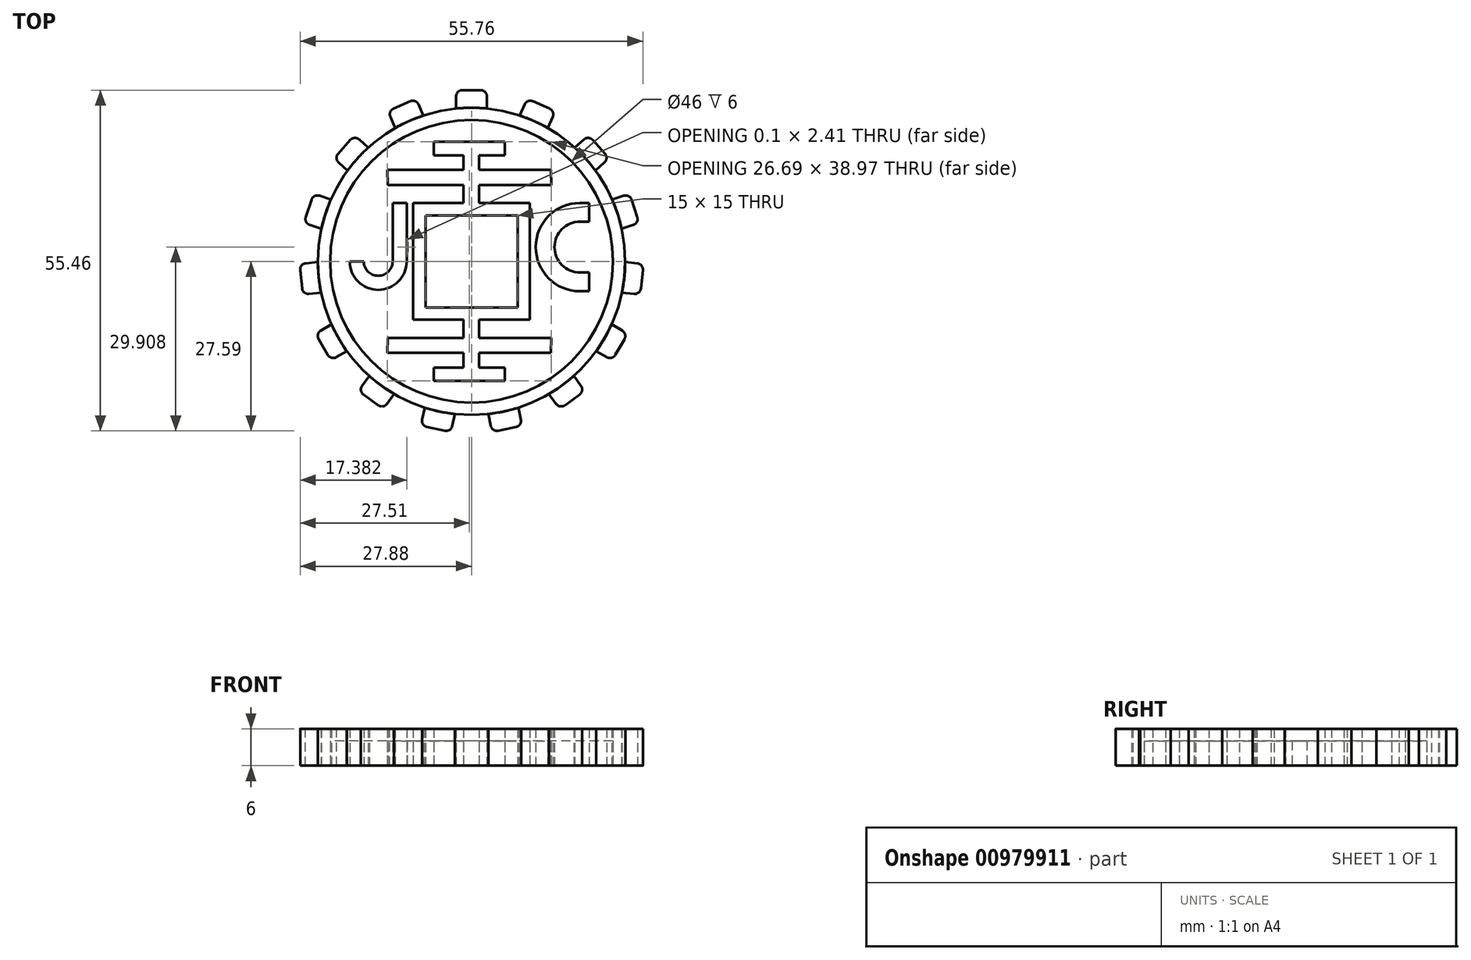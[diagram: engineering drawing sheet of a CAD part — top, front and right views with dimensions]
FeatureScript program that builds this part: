
annotation { "Feature Type Name" : "Feature", "Feature Type Description" : "" }
export const myFeature = defineFeature(function(context is Context, id is Id, definition is map)
    precondition{}
    {
        {
            var Q0;
            Q0=qCreatedBy(makeId("Top.planeOp"),FACE);
            var sketch = newSketch(context, id + "F0", { "sketchPlane" : qUnion([Q0])});
            skLineSegment(sketch, "E0.bottom", {"start": v(7.5, 7.5) * mm, "end": v(-7.5, 7.5) * mm});
            skLineSegment(sketch, "E0.top", {"start": v(7.5, -7.5) * mm, "end": v(-7.5, -7.5) * mm});
            skLineSegment(sketch, "E0.left", {"start": v(7.5, 7.5) * mm, "end": v(7.5, -7.5) * mm});
            skLineSegment(sketch, "E0.right", {"start": v(-7.5, 7.5) * mm, "end": v(-7.5, -7.5) * mm});
            skPoint(sketch, "E0.middle", {"position": v(0, 0) * mm});
            skLineSegment(sketch, "E1.bottom", {"start": v(9.5, 9.5) * mm, "end": v(-9.5, 9.5) * mm});
            skLineSegment(sketch, "E1.top", {"start": v(9.5, -9.5) * mm, "end": v(-9.5, -9.5) * mm});
            skLineSegment(sketch, "E1.left", {"start": v(9.5, 9.5) * mm, "end": v(9.5, -9.5) * mm});
            skLineSegment(sketch, "E1.right", {"start": v(-9.5, 9.5) * mm, "end": v(-9.5, -9.5) * mm});
            skCircle(sketch, "E2", {"center": v(0, 0) * mm, "radius": 25 * mm});
            skCircle(sketch, "E3", {"center": v(0, 0) * mm, "radius": 23 * mm});
            skLineSegment(sketch, "E4", {"start": v(-13.71, 14.88) * mm, "end": v(12.88, 14.88) * mm});
            skLineSegment(sketch, "E5", {"start": v(0, -9.5) * mm, "end": v(0, -9.5) * mm});
            skLineSegment(sketch, "E6", {"start": v(-13.64, 12.45) * mm, "end": v(12.97, 12.45) * mm});
            skLineSegment(sketch, "E7", {"start": v(-13.64, 12.45) * mm, "end": v(-13.71, 14.88) * mm});
            skLineSegment(sketch, "E8", {"start": v(12.88, 14.88) * mm, "end": v(12.97, 12.45) * mm});
            skLineSegment(sketch, "E9.bottom", {"start": v(-1.34, 12.45) * mm, "end": v(1.23, 12.45) * mm});
            skLineSegment(sketch, "E9.top", {"start": v(-1.34, 17.28) * mm, "end": v(1.23, 17.28) * mm});
            skLineSegment(sketch, "E9.left", {"start": v(-1.34, 12.45) * mm, "end": v(-1.34, 17.28) * mm});
            skLineSegment(sketch, "E9.right", {"start": v(1.23, 12.45) * mm, "end": v(1.23, 17.28) * mm});
            skLineSegment(sketch, "E10.bottom", {"start": v(1.23, 17.28) * mm, "end": v(-6.17, 17.28) * mm});
            skLineSegment(sketch, "E10.top", {"start": v(1.23, 19.48) * mm, "end": v(-6.17, 19.48) * mm});
            skLineSegment(sketch, "E10.left", {"start": v(1.23, 17.28) * mm, "end": v(1.23, 19.48) * mm});
            skLineSegment(sketch, "E10.right", {"start": v(-6.17, 17.28) * mm, "end": v(-6.17, 19.48) * mm});
            skLineSegment(sketch, "E11.bottom", {"start": v(-1.34, 17.28) * mm, "end": v(5.39, 17.28) * mm});
            skLineSegment(sketch, "E11.top", {"start": v(-1.34, 19.48) * mm, "end": v(5.39, 19.48) * mm});
            skLineSegment(sketch, "E11.left", {"start": v(-1.34, 17.28) * mm, "end": v(-1.34, 19.48) * mm});
            skLineSegment(sketch, "E11.right", {"start": v(5.39, 17.28) * mm, "end": v(5.39, 19.48) * mm});
            skLineSegment(sketch, "E12", {"start": v(-1.34, 12.45) * mm, "end": v(-1.34, 9.5) * mm});
            skLineSegment(sketch, "E13", {"start": v(1.23, 12.45) * mm, "end": v(1.23, 9.5) * mm});
            skLineSegment(sketch, "E14.MirrorCS", {"start": v(-1.34, -12.45) * mm, "end": v(-1.34, -9.5) * mm});
            skLineSegment(sketch, "E15.MirrorCS", {"start": v(1.23, -12.45) * mm, "end": v(1.23, -9.5) * mm});
            skLineSegment(sketch, "E16.MirrorCS", {"start": v(1.23, -12.45) * mm, "end": v(1.23, -17.28) * mm});
            skLineSegment(sketch, "E17.MirrorCS", {"start": v(-1.34, -12.45) * mm, "end": v(-1.34, -17.28) * mm});
            skLineSegment(sketch, "E18.MirrorCS", {"start": v(-13.64, -12.45) * mm, "end": v(-13.71, -14.88) * mm});
            skLineSegment(sketch, "E19.MirrorCS", {"start": v(12.88, -14.88) * mm, "end": v(12.97, -12.45) * mm});
            skLineSegment(sketch, "E20.MirrorCS", {"start": v(5.39, -17.28) * mm, "end": v(5.39, -19.48) * mm});
            skLineSegment(sketch, "E21.MirrorCS", {"start": v(-6.17, -17.28) * mm, "end": v(-6.17, -19.48) * mm});
            skLineSegment(sketch, "E22.MirrorCS", {"start": v(1.23, -19.48) * mm, "end": v(-6.17, -19.48) * mm});
            skLineSegment(sketch, "E23.MirrorCS", {"start": v(-1.34, -17.28) * mm, "end": v(-1.34, -19.48) * mm});
            skLineSegment(sketch, "E24.MirrorCS", {"start": v(1.23, -17.28) * mm, "end": v(1.23, -19.48) * mm});
            skLineSegment(sketch, "E25.MirrorCS", {"start": v(-1.34, -19.48) * mm, "end": v(5.39, -19.48) * mm});
            skLineSegment(sketch, "E26.MirrorCS", {"start": v(1.23, -17.28) * mm, "end": v(-6.17, -17.28) * mm});
            skLineSegment(sketch, "E27.MirrorCS", {"start": v(-1.34, -17.28) * mm, "end": v(5.39, -17.28) * mm});
            skLineSegment(sketch, "E28.MirrorCS", {"start": v(-13.71, -14.88) * mm, "end": v(12.88, -14.88) * mm});
            skLineSegment(sketch, "E29.MirrorCS", {"start": v(-13.64, -12.45) * mm, "end": v(12.97, -12.45) * mm});
            skLineSegment(sketch, "E30", {"start": v(-12.83, 9.5) * mm, "end": v(-12.83, 0) * mm});
            skLineSegment(sketch, "E31", {"start": v(-10.55, 9.5) * mm, "end": v(-10.55, 0) * mm});
            skLineSegment(sketch, "E32", {"start": v(-12.83, 9.5) * mm, "end": v(-10.55, 9.5) * mm});
            skLineSegment(sketch, "E33", {"start": v(19.13, 9.5) * mm, "end": v(19.13, 6.44) * mm});
            skLineSegment(sketch, "E34", {"start": v(19.13, 9.5) * mm, "end": v(17.63, 9.5) * mm});
            skArc(sketch, "E35", {"start": v(17.63, 9.5) * mm, "mid": v(10.45, 2.32) * mm, "end": v(17.63, -4.86) * mm});
            skArc(sketch, "E36.0", {"start": v(17.63, 6.45) * mm, "mid": v(13.5, 2.32) * mm, "end": v(17.63, -1.82) * mm});
            skLineSegment(sketch, "E37", {"start": v(17.63, 6.45) * mm, "end": v(19.13, 6.44) * mm});
            skLineSegment(sketch, "E38", {"start": v(17.63, -1.82) * mm, "end": v(19.13, -1.82) * mm});
            skLineSegment(sketch, "E39", {"start": v(17.63, -4.86) * mm, "end": v(19.13, -4.86) * mm});
            skLineSegment(sketch, "E40", {"start": v(19.13, -1.82) * mm, "end": v(19.13, -4.86) * mm});
            skArc(sketch, "E41", {"start": v(-10.55, 0) * mm, "mid": v(-15.18, -4.63) * mm, "end": v(-19.82, 0) * mm});
            skArc(sketch, "E42.0", {"start": v(-12.83, 0) * mm, "mid": v(-15.18, -2.35) * mm, "end": v(-17.53, 0) * mm});
            skLineSegment(sketch, "E43", {"start": v(-19.82, 0) * mm, "end": v(-17.53, 0) * mm});
            skLineSegment(sketch, "E44.MirrorCS", {"start": v(19.82, 0) * mm, "end": v(17.53, 0) * mm});
            skArc(sketch, "E45.MirrorCS", {"start": v(12.83, 0) * mm, "mid": v(15.18, -2.35) * mm, "end": v(17.53, 0) * mm});
            skArc(sketch, "E46.MirrorCS", {"start": v(10.55, 0) * mm, "mid": v(15.18, -4.63) * mm, "end": v(19.82, 0) * mm});
            skLineSegment(sketch, "E47.MirrorCS", {"start": v(10.55, 9.5) * mm, "end": v(10.55, 0) * mm});
            skLineSegment(sketch, "E48.MirrorCS", {"start": v(12.83, 9.5) * mm, "end": v(12.83, 0) * mm});
            skLineSegment(sketch, "E49.MirrorCS", {"start": v(12.83, 9.5) * mm, "end": v(10.55, 9.5) * mm});
            skArc(sketch, "E50.MirrorCS", {"start": v(-17.63, 9.5) * mm, "mid": v(-10.45, 2.32) * mm, "end": v(-17.63, -4.86) * mm});
            skArc(sketch, "E51.MirrorCS", {"start": v(-17.63, 6.45) * mm, "mid": v(-13.5, 2.32) * mm, "end": v(-17.63, -1.82) * mm});
            skLineSegment(sketch, "E52.MirrorCS", {"start": v(-17.63, 6.45) * mm, "end": v(-19.13, 6.44) * mm});
            skLineSegment(sketch, "E53.MirrorCS", {"start": v(-19.13, 9.5) * mm, "end": v(-17.63, 9.5) * mm});
            skLineSegment(sketch, "E54.MirrorCS", {"start": v(-19.13, 9.5) * mm, "end": v(-19.13, 6.44) * mm});
            skLineSegment(sketch, "E55.MirrorCS", {"start": v(-19.13, -1.82) * mm, "end": v(-19.13, -4.86) * mm});
            skLineSegment(sketch, "E56.MirrorCS", {"start": v(-17.63, -1.82) * mm, "end": v(-19.13, -1.82) * mm});
            skLineSegment(sketch, "E57.MirrorCS", {"start": v(-17.63, -4.86) * mm, "end": v(-19.13, -4.86) * mm});
            skLineSegment(sketch, "E58.bottom", {"start": v(-2.5, 24.87) * mm, "end": v(0, 24.87) * mm});
            skLineSegment(sketch, "E58.top", {"start": v(-2.5, 27.87) * mm, "end": v(0, 27.87) * mm});
            skLineSegment(sketch, "E58.left", {"start": v(-2.5, 24.87) * mm, "end": v(-2.5, 27.87) * mm});
            skLineSegment(sketch, "E58.right", {"start": v(0, 24.87) * mm, "end": v(0, 27.87) * mm});
            skLineSegment(sketch, "E59.MirrorCS", {"start": v(2.5, 27.87) * mm, "end": v(0, 27.87) * mm});
            skLineSegment(sketch, "E60.MirrorCS", {"start": v(2.5, 24.87) * mm, "end": v(2.5, 27.87) * mm});
            skLineSegment(sketch, "E61.MirrorCS", {"start": v(2.5, 24.87) * mm, "end": v(0, 24.87) * mm});
            skSolve(sketch);
        }
        {
            var Q0;
            {var subQ0=sQuery(id+"F0.wireOp",EDGE,"0sF7ZNBB-Fp62-ajDr-pOHZ-8R5TPl0STRkI");Q0=makeQuery(id+"F0.imprint","IMPRINT",FACE,{"disambiguationData":[TD([[makeQuery(id+"F0.imprint","IMPRINT",EDGE,{"derivedFrom":subQ0}),-1.0]])]});}
            var Q1;
            Q1=makeQuery(id+"F0.imprint","IMPRINT",FACE,{"disambiguationData":[TD([[makeQuery(id+"F0.imprint","IMPRINT",EDGE,{"derivedFrom":sQuery(id+"F0.wireOp",EDGE,"E0.bottom")}),-1.0]])]});
            var Q2;
            {var subQ5=sQuery(id+"F0.wireOp",EDGE,"YXBWEZzm-fCCL-6ggQ-wc8N-nn82RjMW5mCL");Q2=makeQuery(id+"F0.imprint","IMPRINT",FACE,{"disambiguationData":[TD([[makeQuery(id+"F0.imprint","IMPRINT",EDGE,{"derivedFrom":subQ5}),-1.0]])]});}
            var Q3;
            Q3=makeQuery(id+"F0.imprint","IMPRINT",FACE,{"disambiguationData":[TD([[makeQuery(id+"F0.imprint","IMPRINT",EDGE,{"derivedFrom":sQuery(id+"F0.wireOp",EDGE,"E0.bottom")}),-1.0]])]});
            var Q4;
            Q4=makeQuery(id+"F0.imprint","IMPRINT",FACE,{"disambiguationData":[TD([[makeQuery(id+"F0.imprint","IMPRINT",EDGE,{"derivedFrom":sQuery(id+"F0.wireOp",EDGE,"E0.bottom")}),-1.0]])]});
            var Q5;
            Q5=makeQuery(id+"F0.imprint","IMPRINT",FACE,{"disambiguationData":[TD([[makeQuery(id+"F0.imprint","IMPRINT",EDGE,{"derivedFrom":sQuery(id+"F0.wireOp",EDGE,"E0.bottom")}),-1.0]])]});
            var Q6;
            {var subQ5=sQuery(id+"F0.wireOp",EDGE,"E18.MirrorCS");Q6=makeQuery(id+"F0.imprint","IMPRINT",FACE,{"disambiguationData":[TD([[makeQuery(id+"F0.imprint","IMPRINT",EDGE,{"derivedFrom":subQ5}),1.0]])]});}
            var Q7;
            {var subQ0=sQuery(id+"F0.wireOp",EDGE,"E21.MirrorCS");Q7=makeQuery(id+"F0.imprint","IMPRINT",FACE,{"disambiguationData":[TD([[makeQuery(id+"F0.imprint","IMPRINT",EDGE,{"derivedFrom":subQ0}),1.0]])]});}
            var Q8;
            {var subQ0=sQuery(id+"F0.wireOp",EDGE,"E23.MirrorCS");Q8=makeQuery(id+"F0.imprint","IMPRINT",FACE,{"disambiguationData":[TD([[makeQuery(id+"F0.imprint","IMPRINT",EDGE,{"derivedFrom":subQ0}),1.0]])]});}
            var Q9;
            {var subQ1=sQuery(id+"F0.wireOp",EDGE,"E16.MirrorCS");var subQ3=sQuery(id+"F0.wireOp",EDGE,"E28.MirrorCS");var subQ4=makeQuery(id+"F0.imprint","INTERSECT",VERTEX,{"derivedFrom":[subQ1,subQ3]});Q9=makeQuery(id+"F0.imprint","IMPRINT",FACE,{"disambiguationData":[TD([[makeQuery(id+"F0.imprint","IMPRINT",EDGE,{"disambiguationData":[TD([[subQ4,1.0]])],"derivedFrom":subQ3}),-1.0]])]});}
            var Q10;
            {var subQ1=sQuery(id+"F0.wireOp",EDGE,"E16.MirrorCS");var subQ3=sQuery(id+"F0.wireOp",EDGE,"E28.MirrorCS");var subQ4=makeQuery(id+"F0.imprint","INTERSECT",VERTEX,{"derivedFrom":[subQ1,subQ3]});Q10=makeQuery(id+"F0.imprint","IMPRINT",FACE,{"disambiguationData":[TD([[makeQuery(id+"F0.imprint","IMPRINT",EDGE,{"disambiguationData":[TD([[subQ4,1.0]])],"derivedFrom":subQ3}),1.0]])]});}
            var Q11;
            {var subQ0=sQuery(id+"F0.wireOp",EDGE,"E14.MirrorCS");Q11=makeQuery(id+"F0.imprint","IMPRINT",FACE,{"disambiguationData":[TD([[makeQuery(id+"F0.imprint","IMPRINT",EDGE,{"derivedFrom":subQ0}),-1.0]])]});}
            var Q12;
            {var subQ5=sQuery(id+"F0.wireOp",EDGE,"E19.MirrorCS");Q12=makeQuery(id+"F0.imprint","IMPRINT",FACE,{"disambiguationData":[TD([[makeQuery(id+"F0.imprint","IMPRINT",EDGE,{"derivedFrom":subQ5}),1.0]])]});}
            var Q13;
            Q13=makeQuery(id+"F0.imprint","IMPRINT",FACE,{"disambiguationData":[TD([[makeQuery(id+"F0.imprint","IMPRINT",EDGE,{"derivedFrom":sQuery(id+"F0.wireOp",EDGE,"E20.MirrorCS")}),-1.0]])]});
            var Q14;
            {var subQ0=sQuery(id+"F0.wireOp",EDGE,"E12");Q14=makeQuery(id+"F0.imprint","IMPRINT",FACE,{"disambiguationData":[TD([[makeQuery(id+"F0.imprint","IMPRINT",EDGE,{"derivedFrom":subQ0}),1.0]])]});}
            var Q15;
            {var subQ3=sQuery(id+"F0.wireOp",EDGE,"E8");Q15=makeQuery(id+"F0.imprint","IMPRINT",FACE,{"disambiguationData":[TD([[makeQuery(id+"F0.imprint","IMPRINT",EDGE,{"derivedFrom":subQ3}),-1.0]])]});}
            var Q16;
            {var subQ0=sQuery(id+"F0.wireOp",EDGE,"E9.right");var subQ1=sQuery(id+"F0.wireOp",EDGE,"E4");var subQ2=makeQuery(id+"F0.imprint","INTERSECT",VERTEX,{"derivedFrom":[subQ1,subQ0]});Q16=makeQuery(id+"F0.imprint","IMPRINT",FACE,{"disambiguationData":[TD([[makeQuery(id+"F0.imprint","IMPRINT",EDGE,{"disambiguationData":[TD([[subQ2,1.0]])],"derivedFrom":subQ1}),-1.0]])]});}
            var Q17;
            {var subQ0=sQuery(id+"F0.wireOp",EDGE,"E7");Q17=makeQuery(id+"F0.imprint","IMPRINT",FACE,{"disambiguationData":[TD([[makeQuery(id+"F0.imprint","IMPRINT",EDGE,{"derivedFrom":subQ0}),-1.0]])]});}
            var Q18;
            {var subQ5=sQuery(id+"F0.wireOp",EDGE,"E9.top");Q18=makeQuery(id+"F0.imprint","IMPRINT",FACE,{"disambiguationData":[TD([[makeQuery(id+"F0.imprint","IMPRINT",EDGE,{"derivedFrom":subQ5}),-1.0]])]});}
            var Q19;
            Q19=makeQuery(id+"F0.imprint","IMPRINT",FACE,{"disambiguationData":[TD([[makeQuery(id+"F0.imprint","IMPRINT",EDGE,{"derivedFrom":sQuery(id+"F0.wireOp",EDGE,"E10.bottom")}),-1.0]])]});
            var Q20;
            Q20=makeQuery(id+"F0.imprint","IMPRINT",FACE,{"disambiguationData":[TD([[makeQuery(id+"F0.imprint","IMPRINT",EDGE,{"derivedFrom":sQuery(id+"F0.wireOp",EDGE,"E9.top")}),1.0]])]});
            var Q21;
            Q21=makeQuery(id+"F0.imprint","IMPRINT",FACE,{"disambiguationData":[TD([[makeQuery(id+"F0.imprint","IMPRINT",EDGE,{"derivedFrom":sQuery(id+"F0.wireOp",EDGE,"E10.left")}),-1.0]])]});
            var Q22;
            Q22=makeQuery(id+"F0.imprint","IMPRINT",FACE,{"disambiguationData":[TD([[makeQuery(id+"F0.imprint","IMPRINT",EDGE,{"derivedFrom":sQuery(id+"F0.wireOp",EDGE,"E3")}),-1.0]])]});
            var Q23;
            {var subQ5=sQuery(id+"F0.wireOp",EDGE,"E61.MirrorCS");Q23=makeQuery(id+"F0.imprint","IMPRINT",FACE,{"disambiguationData":[TD([[makeQuery(id+"F0.imprint","IMPRINT",EDGE,{"derivedFrom":subQ5}),-1.0]])]});}
            var Q24;
            {var subQ5=sQuery(id+"F0.wireOp",EDGE,"E58.bottom");Q24=makeQuery(id+"F0.imprint","IMPRINT",FACE,{"disambiguationData":[TD([[makeQuery(id+"F0.imprint","IMPRINT",EDGE,{"derivedFrom":subQ5}),1.0]])]});}
            extrude(context, id + "F1", {"entities" : qUnion([Q0, Q1, Q2, Q3, Q4, Q5, Q6, Q7, Q8, Q9, Q10, Q11, Q12, Q13, Q14, Q15, Q16, Q17, Q18, Q19, Q20, Q21, Q22, Q23, Q24]), "depth" : 6 * mm, "offsetDistance" : 25.4 * mm});
        }
        {
            var Q0;
            {var subQ40=sQuery(id+"F0.wireOp",EDGE,"E1.left");Q0=makeQuery(id+"F0.imprint","IMPRINT",FACE,{"disambiguationData":[TD([[makeQuery(id+"F0.imprint","IMPRINT",EDGE,{"derivedFrom":subQ40}),1.0]])]});}
            var Q1;
            {var subQ3=sQuery(id+"F0.wireOp",EDGE,"E52.MirrorCS");Q1=makeQuery(id+"F0.imprint","IMPRINT",FACE,{"disambiguationData":[TD([[makeQuery(id+"F0.imprint","IMPRINT",EDGE,{"derivedFrom":subQ3}),-1.0]])]});}
            var Q2;
            {var subQ8=sQuery(id+"F0.wireOp",EDGE,"E56.MirrorCS");Q2=makeQuery(id+"F0.imprint","IMPRINT",FACE,{"disambiguationData":[TD([[makeQuery(id+"F0.imprint","IMPRINT",EDGE,{"derivedFrom":subQ8}),1.0]])]});}
            var Q3;
            {var subQ0=sQuery(id+"F0.wireOp",EDGE,"E41");var subQ1=sQuery(id+"F0.wireOp",EDGE,"E31");var subQ2=makeQuery(id+"F0.imprint","INTERSECT",VERTEX,{"derivedFrom":[subQ1,subQ0]});Q3=makeQuery(id+"F0.imprint","IMPRINT",FACE,{"disambiguationData":[TD([[makeQuery(id+"F0.imprint","IMPRINT",EDGE,{"disambiguationData":[TD([[subQ2,1.0]])],"derivedFrom":subQ1}),-1.0]])]});}
            var Q4;
            {var subQ3=sQuery(id+"F0.wireOp",EDGE,"E32");Q4=makeQuery(id+"F0.imprint","IMPRINT",FACE,{"disambiguationData":[TD([[makeQuery(id+"F0.imprint","IMPRINT",EDGE,{"derivedFrom":subQ3}),-1.0]])]});}
            var Q5;
            {var subQ4=sQuery(id+"F0.wireOp",EDGE,"E43");Q5=makeQuery(id+"F0.imprint","IMPRINT",FACE,{"disambiguationData":[TD([[makeQuery(id+"F0.imprint","IMPRINT",EDGE,{"derivedFrom":subQ4}),-1.0]])]});}
            var Q6;
            {var subQ5=sQuery(id+"F0.wireOp",EDGE,"E57.MirrorCS");Q6=makeQuery(id+"F0.imprint","IMPRINT",FACE,{"disambiguationData":[TD([[makeQuery(id+"F0.imprint","IMPRINT",EDGE,{"derivedFrom":subQ5}),-1.0]])]});}
            var Q7;
            {var subQ0=sQuery(id+"F0.wireOp",EDGE,"E50.MirrorCS");var subQ1=sQuery(id+"F0.wireOp",EDGE,"E31");var subQ2=makeQuery(id+"F0.imprint","INTERSECT",VERTEX,{"disambiguationData":[OD(0.0)],"derivedFrom":[subQ1,subQ0]});Q7=makeQuery(id+"F0.imprint","IMPRINT",FACE,{"disambiguationData":[TD([[makeQuery(id+"F0.imprint","IMPRINT",EDGE,{"disambiguationData":[TD([[subQ2,1.0]])],"derivedFrom":subQ1}),1.0]])]});}
            var Q8;
            {var subQ0=sQuery(id+"F0.wireOp",EDGE,"E38");Q8=makeQuery(id+"F0.imprint","IMPRINT",FACE,{"disambiguationData":[TD([[makeQuery(id+"F0.imprint","IMPRINT",EDGE,{"derivedFrom":subQ0}),-1.0]])]});}
            var Q9;
            {var subQ0=sQuery(id+"F0.wireOp",EDGE,"E47.MirrorCS");var subQ1=sQuery(id+"F0.wireOp",EDGE,"E35");var subQ2=makeQuery(id+"F0.imprint","INTERSECT",VERTEX,{"disambiguationData":[OD(1.0)],"derivedFrom":[subQ1,subQ0]});Q9=makeQuery(id+"F0.imprint","IMPRINT",FACE,{"disambiguationData":[TD([[makeQuery(id+"F0.imprint","IMPRINT",EDGE,{"disambiguationData":[TD([[subQ2,-1.0]])],"derivedFrom":subQ1}),-1.0]])]});}
            var Q10;
            Q10=makeQuery(id+"F0.imprint","IMPRINT",FACE,{"disambiguationData":[TD([[makeQuery(id+"F0.imprint","IMPRINT",EDGE,{"derivedFrom":sQuery(id+"F0.wireOp",EDGE,"E33")}),-1.0]])]});
            var Q11;
            {var subQ0=sQuery(id+"F0.wireOp",EDGE,"E47.MirrorCS");var subQ1=sQuery(id+"F0.wireOp",EDGE,"E35");var subQ2=makeQuery(id+"F0.imprint","INTERSECT",VERTEX,{"disambiguationData":[OD(0.0)],"derivedFrom":[subQ1,subQ0]});Q11=makeQuery(id+"F0.imprint","IMPRINT",FACE,{"disambiguationData":[TD([[makeQuery(id+"F0.imprint","IMPRINT",EDGE,{"disambiguationData":[TD([[subQ2,-1.0]])],"derivedFrom":subQ1}),1.0]])]});}
            var Q12;
            {var subQ5=sQuery(id+"F0.wireOp",EDGE,"E49.MirrorCS");Q12=makeQuery(id+"F0.imprint","IMPRINT",FACE,{"disambiguationData":[TD([[makeQuery(id+"F0.imprint","IMPRINT",EDGE,{"derivedFrom":subQ5}),1.0]])]});}
            var Q13;
            {var subQ1=sQuery(id+"F0.wireOp",EDGE,"E38");Q13=makeQuery(id+"F0.imprint","IMPRINT",FACE,{"disambiguationData":[TD([[makeQuery(id+"F0.imprint","IMPRINT",EDGE,{"derivedFrom":subQ1}),1.0]])]});}
            var Q14;
            {var subQ0=sQuery(id+"F0.wireOp",EDGE,"E39");Q14=makeQuery(id+"F0.imprint","IMPRINT",FACE,{"disambiguationData":[TD([[makeQuery(id+"F0.imprint","IMPRINT",EDGE,{"derivedFrom":subQ0}),1.0]])]});}
            extrude(context, id + "F2", {"entities" : qUnion([Q0, Q1, Q2, Q3, Q4, Q5, Q6, Q7, Q8, Q9, Q10, Q11, Q12, Q13, Q14]), "depth" : 4 * mm, "offsetDistance" : 25.4 * mm});
        }
        {
            var Q0;
            {var subQ3=sQuery(id+"F0.wireOp",EDGE,"E32");Q0=makeQuery(id+"F0.imprint","IMPRINT",FACE,{"disambiguationData":[TD([[makeQuery(id+"F0.imprint","IMPRINT",EDGE,{"derivedFrom":subQ3}),-1.0]])]});}
            var Q1;
            {var subQ8=sQuery(id+"F0.wireOp",EDGE,"E56.MirrorCS");Q1=makeQuery(id+"F0.imprint","IMPRINT",FACE,{"disambiguationData":[TD([[makeQuery(id+"F0.imprint","IMPRINT",EDGE,{"derivedFrom":subQ8}),1.0]])]});}
            var Q2;
            {var subQ0=sQuery(id+"F0.wireOp",EDGE,"E41");var subQ1=sQuery(id+"F0.wireOp",EDGE,"E31");var subQ2=makeQuery(id+"F0.imprint","INTERSECT",VERTEX,{"derivedFrom":[subQ1,subQ0]});Q2=makeQuery(id+"F0.imprint","IMPRINT",FACE,{"disambiguationData":[TD([[makeQuery(id+"F0.imprint","IMPRINT",EDGE,{"disambiguationData":[TD([[subQ2,1.0]])],"derivedFrom":subQ1}),-1.0]])]});}
            var Q3;
            {var subQ4=sQuery(id+"F0.wireOp",EDGE,"E43");Q3=makeQuery(id+"F0.imprint","IMPRINT",FACE,{"disambiguationData":[TD([[makeQuery(id+"F0.imprint","IMPRINT",EDGE,{"derivedFrom":subQ4}),-1.0]])]});}
            var Q4;
            Q4=makeQuery(id+"F0.imprint","IMPRINT",FACE,{"disambiguationData":[TD([[makeQuery(id+"F0.imprint","IMPRINT",EDGE,{"derivedFrom":sQuery(id+"F0.wireOp",EDGE,"E33")}),-1.0]])]});
            var Q5;
            {var subQ0=sQuery(id+"F0.wireOp",EDGE,"E38");Q5=makeQuery(id+"F0.imprint","IMPRINT",FACE,{"disambiguationData":[TD([[makeQuery(id+"F0.imprint","IMPRINT",EDGE,{"derivedFrom":subQ0}),-1.0]])]});}
            var Q6;
            {var subQ0=sQuery(id+"F0.wireOp",EDGE,"E39");Q6=makeQuery(id+"F0.imprint","IMPRINT",FACE,{"disambiguationData":[TD([[makeQuery(id+"F0.imprint","IMPRINT",EDGE,{"derivedFrom":subQ0}),1.0]])]});}
            var Q7;
            {var subQ0=sQuery(id+"F0.wireOp",EDGE,"E47.MirrorCS");var subQ1=sQuery(id+"F0.wireOp",EDGE,"E35");var subQ2=makeQuery(id+"F0.imprint","INTERSECT",VERTEX,{"disambiguationData":[OD(0.0)],"derivedFrom":[subQ1,subQ0]});Q7=makeQuery(id+"F0.imprint","IMPRINT",FACE,{"disambiguationData":[TD([[makeQuery(id+"F0.imprint","IMPRINT",EDGE,{"disambiguationData":[TD([[subQ2,-1.0]])],"derivedFrom":subQ1}),1.0]])]});}
            extrude(context, id + "F3", {"entities" : qUnion([Q0, Q1, Q2, Q3, Q4, Q5, Q6, Q7]), "depth" : 6 * mm, "offsetDistance" : 25.4 * mm});
        }
        {
            var Q0;
            Q0=qCreatedBy(makeId("Right.planeOp"),FACE);
            var sketch = newSketch(context, id + "F4", { "sketchPlane" : qUnion([Q0])});
            skLineSegment(sketch, "E62", {"start": v(0, 0) * mm, "end": v(0, 14.58) * mm});
            skSolve(sketch);
        }
        {
            var Q0;
            {var subQ5=sQuery(id+"F0.wireOp",EDGE,"E59.MirrorCS");Q0=makeQuery(id+"F0.imprint","IMPRINT",FACE,{"disambiguationData":[TD([[makeQuery(id+"F0.imprint","IMPRINT",EDGE,{"derivedFrom":subQ5}),1.0]])]});}
            var Q1;
            {var subQ5=sQuery(id+"F0.wireOp",EDGE,"E58.top");Q1=makeQuery(id+"F0.imprint","IMPRINT",FACE,{"disambiguationData":[TD([[makeQuery(id+"F0.imprint","IMPRINT",EDGE,{"derivedFrom":subQ5}),-1.0]])]});}
            extrude(context, id + "F5", {"entities" : qUnion([Q0, Q1]), "depth" : 6 * mm, "offsetDistance" : 25.4 * mm});
        }
        {
            var Q0;
            Q0=makeQuery(id+"F5.opExtrude","SWEPT_EDGE",EDGE,{"disambiguationData":[OSD([sQuery(id+"F0.wireOp",EDGE,"E58.top"),sQuery(id+"F0.wireOp",EDGE,"E58.left")])]});
            var Q1;
            Q1=makeQuery(id+"F5.opExtrude","SWEPT_EDGE",EDGE,{"disambiguationData":[OSD([sQuery(id+"F0.wireOp",EDGE,"E59.MirrorCS"),sQuery(id+"F0.wireOp",EDGE,"E60.MirrorCS")])]});
            fillet(context, id + "F6", {"entities" : qUnion([Q0, Q1]), "tangentPropagation" : true, "radius" : 1 * mm, "defaultsChanged" : true, "vertexSettings" : [], "allowEdgeOverflow" : false});
        }
        {
            var Q0;
            Q0=makeQuery(id+"F5.opExtrude","SWEPT_BODY",BODY,{"disambiguationData":[OSD([sQuery(id+"F0.wireOp",EDGE,"E2"),sQuery(id+"F0.wireOp",EDGE,"E58.top"),sQuery(id+"F0.wireOp",EDGE,"E58.left"),sQuery(id+"F0.wireOp",EDGE,"E59.MirrorCS"),sQuery(id+"F0.wireOp",EDGE,"E60.MirrorCS")])]});
            var Q1;
            Q1=sQuery(id+"F4.wireOp",EDGE,"E62");
            circularPattern(context, id + "F7", {"entities" : qUnion([Q0]), "axis" : qUnion([Q1]), "angle" : 360 * degree, "instanceCount" : 15, "equalSpace" : true});
        }
    });
